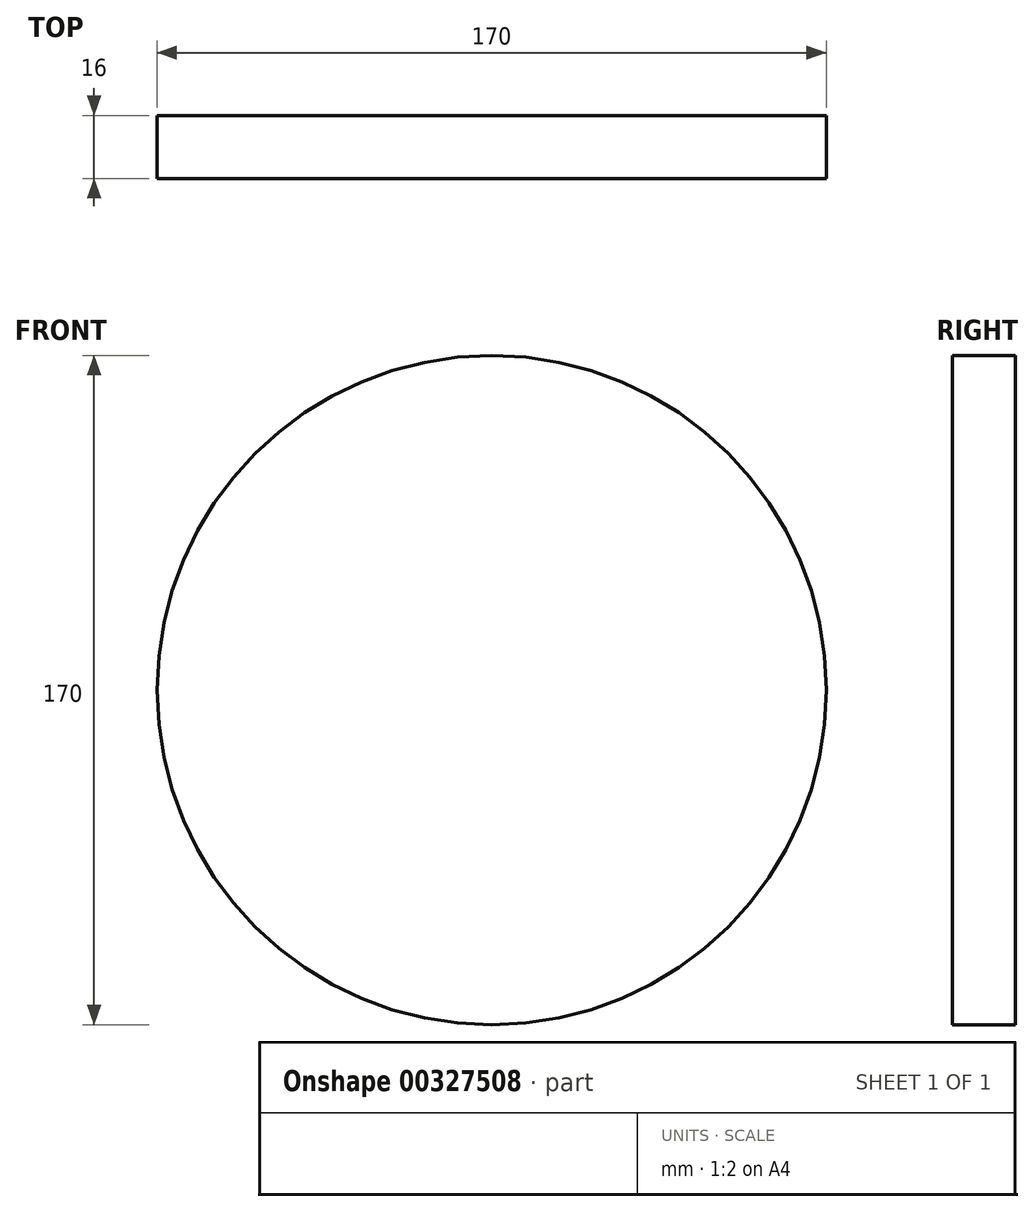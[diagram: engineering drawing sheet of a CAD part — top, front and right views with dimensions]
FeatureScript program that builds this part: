
annotation { "Feature Type Name" : "Feature", "Feature Type Description" : "" }
export const myFeature = defineFeature(function(context is Context, id is Id, definition is map)
    precondition{}
    {
        {
            var Q0;
            Q0=qCreatedBy(makeId("Front.planeOp"),FACE);
            var sketch = newSketch(context, id + "F0", { "sketchPlane" : qUnion([Q0])});
            skCircle(sketch, "E0", {"center": v(0, 0) * mm, "radius": 85 * mm});
            skSolve(sketch);
        }
        {
            var Q0;
            Q0=makeQuery(id+"F0.imprint","IMPRINT",FACE,{"disambiguationData":[TD([[makeQuery(id+"F0.imprint","IMPRINT",EDGE,{"derivedFrom":sQuery(id+"F0.wireOp",EDGE,"E0")}),1.0]])]});
            extrude(context, id + "F1", {"entities" : qUnion([Q0]), "depth" : 16 * mm});
        }
    });
